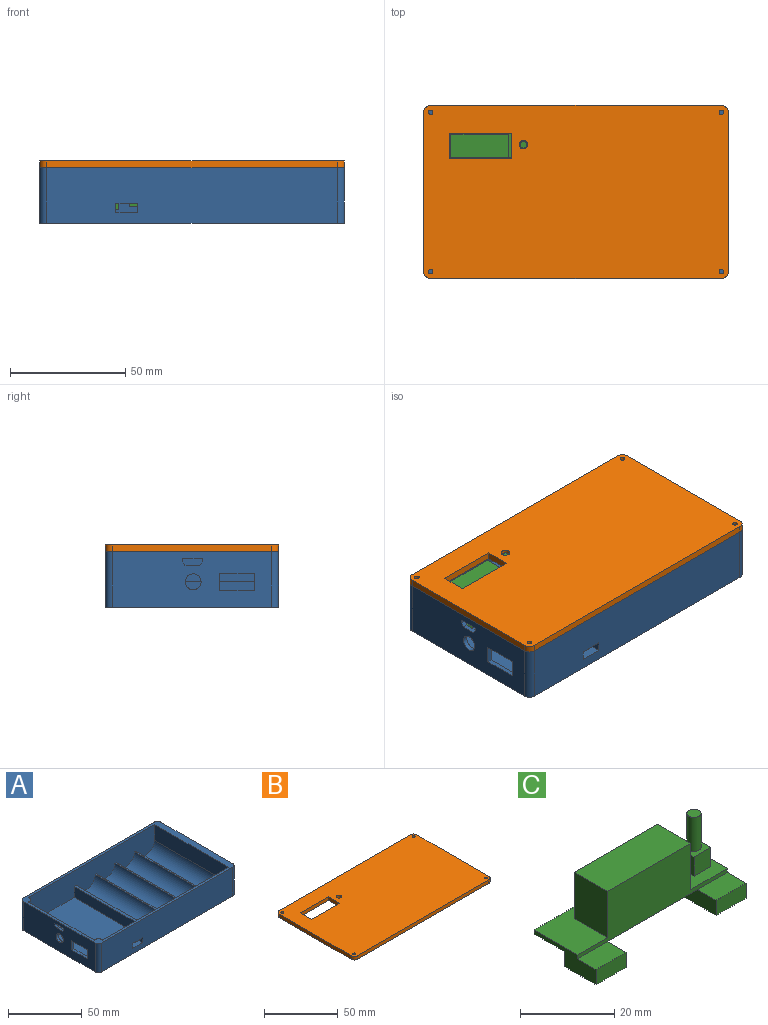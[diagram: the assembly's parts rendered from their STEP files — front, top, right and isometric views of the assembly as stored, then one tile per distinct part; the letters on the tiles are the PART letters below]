
ASSEMBLY  parts=3 mates=4
PART A: 49 faces, bbox 132x75x24 mm
  f0: plane 121.17x22mm, normal (0,1,0), area 2274.9mm2, adj f4,f6,f10,f11,f12,f13,f14,f15
  f1: plane 126x24mm, normal (0,-1,0), area 2986mm2, adj f6,f9,f21,f22,f37,f38,f39,f40
  f2: plane 63.34x22mm, normal (1,0,0), area 1219.6mm2, adj f4,f6,f24,f25,f26,f27,f28,f29
  f3: plane 69x24mm, normal (-1,0,0), area 1482mm2, adj f6,f9,f20,f21,f26,f27,f28,f29
  f4: plane 71x47.94mm, normal (0,0,1), area 3323.8mm2, adj f0,f2,f5,f12,f24,f25,f42,f43
  f5: plane 121.17x22mm, normal (0,-1,0), area 2437.9mm2, adj f4,f6,f10,f11,f12,f13,f14,f15
  f6: plane 132x75mm, normal (0,0,1), area 1045.2mm2, adj f0,f1,f2,f3,f5,f7,f8,f11
  f7: plane 126x24mm, normal (0,1,0), area 3024mm2, adj f6,f9,f20,f23
  f8: plane 69x24mm, normal (1,0,0), area 1656mm2, adj f6,f9,f22,f23
  f9: plane 132x75mm, normal (0,0,-1), area 9892.3mm2, adj f1,f3,f7,f8,f20,f21,f22,f23
  f10: cylinder r=9mm len=71mm, axis (0,-1,0), area 1906.7mm2, adj f0,f5,f11,f18
  f11: plane 71x13.1mm, normal (-1,0,0), area 930.1mm2, adj f0,f5,f6,f10
  f12: plane 71x8.9mm, normal (-1,0,0), area 631.9mm2, adj f0,f4,f5,f13
  f13: plane 71x2.11mm, normal (0,0,1), area 150mm2, adj f0,f5,f12,f14
  f14: cylinder r=9mm len=71mm, axis (0,-1,0), area 1906.7mm2, adj f0,f5,f13,f15
  f15: plane 71x1.06mm, normal (0,0,1), area 75mm2, adj f0,f5,f14,f16
  f16: cylinder r=9mm len=71mm, axis (0,-1,0), area 1906.7mm2, adj f0,f5,f15,f17
  f17: plane 71x1.06mm, normal (0,0,1), area 75mm2, adj f0,f5,f16,f19
  f18: plane 71x1.06mm, normal (0,0,1), area 75mm2, adj f0,f5,f10,f19
  f19: cylinder r=9mm len=71mm, axis (0,-1,0), area 1906.7mm2, adj f0,f5,f17,f18
  f20: cylinder r=3mm len=24mm, axis (0,0,1), area 113.1mm2, adj f3,f6,f7,f9
  f21: cylinder r=3mm len=24mm, axis (0,0,-1), area 113.1mm2, adj f1,f3,f6,f9
  f22: cylinder r=3mm len=24mm, axis (0,0,1), area 113.1mm2, adj f1,f6,f8,f9
  f23: cylinder r=3mm len=24mm, axis (0,0,-1), area 113.1mm2, adj f6,f7,f8,f9
  f24: cylinder r=3mm len=22mm, axis (0,0,-1), area 148.5mm2, adj f2,f4,f5,f6
  f25: cylinder r=3mm len=22mm, axis (0,0,-1), area 148.5mm2, adj f0,f2,f4,f6
  f26: plane 2x1.41mm, normal (0,1,0), area 2.8mm2, adj f2,f3,f27,f31
  f27: plane 8.58x2mm, normal (0,0,-1), area 17.2mm2, adj f2,f3,f26,f28
  f28: plane 2x1.41mm, normal (0,-1,0), area 2.8mm2, adj f2,f3,f27,f29
  f29: plane 2x1.59mm, normal (0,-0.84,0.55), area 3.8mm2, adj f2,f3,f28,f30
  f30: plane 6.5x2mm, normal (0,0,1), area 13mm2, adj f2,f3,f29,f31
  f31: plane 2x1.59mm, normal (0,0.84,0.55), area 3.8mm2, adj f2,f3,f26,f30
  f32: cylinder r=3.45mm len=6.9mm, axis (-1,0,0), area 43.4mm2, adj f2,f3
  f33: plane 15x2mm, normal (0,0,1), area 30mm2, adj f2,f3,f34,f36
  f34: plane 7.5x2mm, normal (0,1,0), area 15mm2, adj f2,f3,f33,f35
  f35: plane 15x2mm, normal (0,0,-1), area 30mm2, adj f2,f3,f34,f36
  f36: plane 7.5x2mm, normal (0,-1,0), area 15mm2, adj f2,f3,f33,f35
  f37: plane 4x4mm, normal (1,0,0), area 16mm2, adj f1,f38,f40,f42
  f38: plane 9.5x4mm, normal (0,0,1), area 38mm2, adj f1,f37,f39,f42
  f39: plane 4x4mm, normal (-1,0,0), area 16mm2, adj f1,f38,f40,f42
  f40: plane 9.5x4mm, normal (0,0,-1), area 38mm2, adj f1,f37,f39,f42
  f41: plane 19.17x5mm, normal (0,0,1), area 52.4mm2, adj f0,f42,f43,f44,f45,f46,f47,f48
  f42: plane 14.5x8.5mm, normal (0,1,0), area 85.3mm2, adj f4,f37,f38,f39,f40,f41,f43,f46
  f43: plane 8.5x3mm, normal (1,0,0), area 25.5mm2, adj f4,f41,f42,f45
  f44: plane 8.5x5mm, normal (-1,0,0), area 42.5mm2, adj f0,f4,f41,f45
  f45: plane 8.5x2.2mm, normal (0,1,0), area 18.7mm2, adj f4,f41,f43,f44
  f46: plane 8.5x3mm, normal (-1,0,0), area 25.5mm2, adj f4,f41,f42,f48
  f47: plane 8.5x5mm, normal (1,0,0), area 42.5mm2, adj f0,f4,f41,f48
  f48: plane 8.5x2.47mm, normal (0,1,0), area 21mm2, adj f4,f41,f46,f47
PART B: 19 faces, bbox 132x75x3 mm
  f0: plane 132x75mm, normal (0,0,1), area 9572.2mm2, adj f2,f3,f4,f5,f6,f7,f8,f9
  f1: plane 132x75mm, normal (0,0,-1), area 9572.2mm2, adj f2,f3,f4,f5,f6,f7,f8,f9
  f2: plane 126x3mm, normal (0,1,0), area 378mm2, adj f0,f1,f6,f9
  f3: plane 69x3mm, normal (-1,0,0), area 207mm2, adj f0,f1,f6,f7
  f4: plane 126x3mm, normal (0,-1,0), area 378mm2, adj f0,f1,f7,f8
  f5: plane 69x3mm, normal (1,0,0), area 207mm2, adj f0,f1,f8,f9
  f6: cylinder r=3mm len=3mm, axis (0,0,1), area 14.1mm2, adj f0,f1,f2,f3
  f7: cylinder r=3mm len=3mm, axis (0,0,-1), area 14.1mm2, adj f0,f1,f3,f4
  f8: cylinder r=3mm len=3mm, axis (0,0,1), area 14.1mm2, adj f0,f1,f4,f5
  f9: cylinder r=3mm len=3mm, axis (0,0,-1), area 14.1mm2, adj f0,f1,f2,f5
  f10: plane 27x3mm, normal (0,-1,0), area 81mm2, adj f0,f1,f11,f13
  f11: plane 11x3mm, normal (1,0,0), area 33mm2, adj f0,f1,f10,f12
  f12: plane 27x3mm, normal (0,1,0), area 81mm2, adj f0,f1,f11,f13
  f13: plane 11x3mm, normal (-1,0,0), area 33mm2, adj f0,f1,f10,f12
  f14: cylinder r=1mm len=3mm, axis (0,0,1), area 18.8mm2, adj f0,f1
  f15: cylinder r=1.83mm len=3.66mm, axis (0,0,1), area 34.5mm2, adj f0,f1
  f16: cylinder r=1mm len=3mm, axis (0,0,1), area 18.8mm2, adj f0,f1
  f17: cylinder r=1mm len=3mm, axis (0,0,1), area 18.8mm2, adj f0,f1
  f18: cylinder r=1mm len=3mm, axis (0,0,1), area 18.8mm2, adj f0,f1
PART C: 31 faces, bbox 45x18.6x19.8 mm
  f0: plane 45x13mm, normal (0,0,1), area 310mm2, adj f2,f3,f4,f5,f20,f21,f22,f24
  f1: plane 45x13mm, normal (0,0,-1), area 337.5mm2, adj f2,f3,f4,f5,f6,f7,f8,f12
  f2: plane 45x13mm, normal (0,-1,0), area 345mm2, adj f0,f1,f3,f5,f10,f15,f20,f21
  f3: plane 18.6x4.9mm, normal (1,0,0), area 50.4mm2, adj f0,f1,f2,f4,f10,f11,f13,f14
  f4: plane 45x6mm, normal (0,1,0), area 157.5mm2, adj f0,f1,f3,f5,f6,f7,f9
  f5: plane 18.6x4.9mm, normal (-1,0,0), area 50.4mm2, adj f0,f1,f2,f4,f15,f16,f18,f19
  f6: plane 7.8x5mm, normal (-1,0,0), area 39mm2, adj f1,f4,f8,f9
  f7: plane 7.8x5mm, normal (1,0,0), area 39mm2, adj f1,f4,f8,f9
  f8: plane 22.5x5mm, normal (0,-1,0), area 112.5mm2, adj f1,f6,f7,f9
  f9: plane 22.5x7.8mm, normal (0,0,-1), area 175.5mm2, adj f4,f6,f7,f8
  f10: plane 9x5.6mm, normal (0,0,1), area 50.4mm2, adj f2,f3,f11,f12
  f11: plane 9x3.9mm, normal (0,-1,0), area 35.1mm2, adj f3,f10,f12,f14
  f12: plane 9.6x3.9mm, normal (-1,0,0), area 37.4mm2, adj f1,f10,f11,f13,f14
  f13: plane 9x3.9mm, normal (0,1,0), area 35.1mm2, adj f1,f3,f12,f14
  f14: plane 9.6x9mm, normal (0,0,-1), area 86.4mm2, adj f3,f11,f12,f13
  f15: plane 9x5.6mm, normal (0,0,1), area 50.4mm2, adj f2,f5,f17,f18
  f16: plane 9x3.9mm, normal (0,1,0), area 35.1mm2, adj f1,f5,f17,f19
  f17: plane 9.6x3.9mm, normal (1,0,0), area 37.4mm2, adj f1,f15,f16,f18,f19
  f18: plane 9x3.9mm, normal (0,-1,0), area 35.1mm2, adj f5,f15,f17,f19
  f19: plane 9.6x9mm, normal (0,0,-1), area 86.4mm2, adj f5,f16,f17,f18
  f20: plane 12x10mm, normal (-1,0,0), area 120mm2, adj f0,f2,f22,f23
  f21: plane 12x10mm, normal (1,0,0), area 120mm2, adj f0,f2,f22,f23
  f22: plane 25x12mm, normal (0,1,0), area 300mm2, adj f0,f20,f21,f23
  f23: plane 25x10mm, normal (0,0,1), area 250mm2, adj f2,f20,f21,f22
  f24: plane 5x5mm, normal (0,-1,0), area 25mm2, adj f0,f25,f27,f28
  f25: plane 5x5mm, normal (1,0,0), area 25mm2, adj f0,f24,f26,f28
  f26: plane 5x5mm, normal (0,1,0), area 25mm2, adj f0,f25,f27,f28
  f27: plane 5x5mm, normal (-1,0,0), area 25mm2, adj f0,f24,f26,f28
  f28: plane 5x5mm, normal (0,0,1), area 17.9mm2, adj f24,f25,f26,f27,f29
  f29: cylinder r=1.5mm len=8.8mm, axis (0,0,-1), area 82.9mm2, adj f28,f30
  f30: plane 3x3mm, normal (0,0,1), area 7.1mm2, adj f29
PLACE A t=(0,0,17.12)mm
PLACE B t=(-66,37.5,41.12)mm
PLACE C t=(-84.24,52.5,28.12)mm
MATE planar C.f23 <-> A.f21  axis (0,0,1) through (-107.74,57.5,41.12)mm
MATE planar B.f2 <-> A.f7  axis (0,1,0) through (-66,75,42.62)mm
MATE planar B.f3 <-> A.f3  axis (-1,0,0) through (-132,37.5,42.62)mm
MATE planar B.f1 <-> A.f6  axis (0,0,-1) through (-64.69,36.86,41.12)mm
